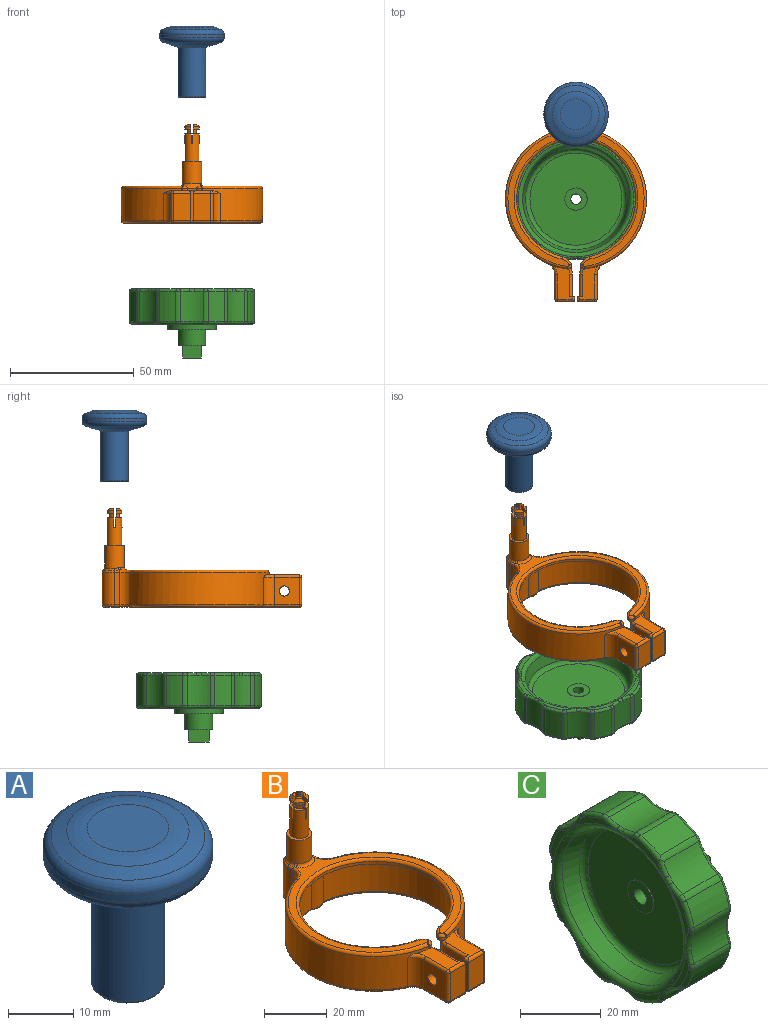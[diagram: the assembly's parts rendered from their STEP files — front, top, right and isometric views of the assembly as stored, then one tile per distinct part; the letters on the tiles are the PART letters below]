
ASSEMBLY  parts=3 mates=2
PART A: 20 faces, bbox 28.1x28.1x29 mm
  f0: cylinder r=4.1mm len=8.2mm, axis (0,0,-1), area 195.8mm2, adj f13,f14
  f1: plane 10.4x10.4mm, normal (0,0,-1), area 21.3mm2, adj f14,f15
  f2: cylinder r=5.6mm len=19.8mm, axis (0,0,-1), area 696.6mm2, adj f15,f16
  f3: sphere r=30mm, area 343.4mm2, adj f16,f17
  f4: cylinder r=13mm len=26mm, axis (0,0,-1), area 122.3mm2, adj f17,f18
  f5: sphere r=30mm, area 171.9mm2, adj f18,f19
  f6: plane 12.49x12.49mm, normal (0,0,1), area 122.5mm2, adj f19
  f7: plane 6.2x6.2mm, normal (0,0,-1), area 30.2mm2, adj f8
  f8: cylinder r=3.1mm len=6.2mm, axis (0,0,-1), area 62.3mm2, adj f7,f9
  f9: plane 6.2x6.2mm, normal (0,0,1), area 16.3mm2, adj f8,f10
  f10: cylinder r=2.1mm len=4.2mm, axis (0,0,-1), area 10.6mm2, adj f9,f11
  f11: cone r=3.1mm half-angle=45deg, axis (0,0,-1), area 23.1mm2, adj f10,f12
  f12: cylinder r=3.1mm len=11mm, axis (0,0,-1), area 214.3mm2, adj f11,f13
  f13: plane 8.2x8.2mm, normal (0,0,-1), area 22.6mm2, adj f0,f12
  f14: torus R=4.5mm, axis (0,0,-1), area 16.8mm2, adj f0,f1
  f15: torus R=5.2mm, axis (0,0,-1), area 21.5mm2, adj f1,f2
  f16: torus R=6mm, axis (0,0,1), area 19.7mm2, adj f2,f3
  f17: torus R=11mm, axis (0,0,1), area 184.4mm2, adj f3,f4
  f18: torus R=11mm, axis (0,0,-1), area 184.4mm2, adj f4,f5
  f19: torus R=6.24mm, axis (0,0,-1), area 156mm2, adj f5,f6
PART B: 154 faces, bbox 61.7x81x40.1 mm
  f0: plane 2.34x2.34mm, normal (0,0,-1), area 2.7mm2, adj f3,f6,f138,f139
  f1: plane 2.34x2.34mm, normal (0,0,-1), area 2.7mm2, adj f4,f7,f142,f143
  f2: plane 2.34x2.34mm, normal (0,0,-1), area 2.7mm2, adj f5,f8,f144,f145
  f3: cylinder r=2mm len=2mm, axis (0,0,-1), area 3.9mm2, adj f0,f27,f138,f139,f150,f152
  f4: cylinder r=2mm len=2mm, axis (0,0,-1), area 3.9mm2, adj f1,f28,f142,f143,f146,f147
  f5: cylinder r=2mm len=2mm, axis (0,0,-1), area 3.9mm2, adj f2,f29,f144,f145,f151,f153
  f6: cylinder r=3mm len=2.34mm, axis (0,0,-1), area 3.5mm2, adj f0,f9,f138,f139
  f7: cylinder r=3mm len=2.34mm, axis (0,0,-1), area 3.5mm2, adj f1,f10,f142,f143
  f8: cylinder r=3mm len=2.34mm, axis (0,0,-1), area 3.5mm2, adj f2,f11,f144,f145
  f9: cone r=2mm half-angle=45deg, axis (0,0,-1), area 3.8mm2, adj f6,f12,f138,f139
  f10: cone r=2mm half-angle=45deg, axis (0,0,-1), area 3.8mm2, adj f7,f13,f142,f143
  f11: cone r=2mm half-angle=45deg, axis (0,0,-1), area 3.8mm2, adj f8,f14,f144,f145
  f12: plane 1.31x1.31mm, normal (0,0,1), area 1mm2, adj f9,f25,f138,f139
  f13: plane 1.31x1.31mm, normal (0,0,1), area 1mm2, adj f10,f24,f142,f143
  f14: plane 1.31x1.31mm, normal (0,0,1), area 1mm2, adj f11,f23,f144,f145
  f15: plane 4x1.77mm, normal (0,1,0), area 7.1mm2, adj f25,f26,f27,f136
  f16: plane 4x1.77mm, normal (1,0,0), area 7.1mm2, adj f25,f26,f27,f136
  f17: plane 4x1.77mm, normal (-1,0,0), area 7.1mm2, adj f26,f131,f136,f137
  f18: plane 4x1.77mm, normal (0,1,0), area 7.1mm2, adj f26,f131,f136,f137
  f19: plane 4x1.77mm, normal (0,-1,0), area 7.1mm2, adj f24,f26,f28,f136
  f20: plane 4x1.77mm, normal (-1,0,0), area 7.1mm2, adj f24,f26,f28,f136
  f21: plane 4x1.77mm, normal (1,0,0), area 7.1mm2, adj f23,f26,f29,f136
  f22: plane 4x1.77mm, normal (0,-1,0), area 7.1mm2, adj f23,f26,f29,f136
  f23: cylinder r=1.25mm len=8mm, axis (0,0,1), area 8.7mm2, adj f14,f21,f22,f29,f136,f144,f145,f151
  f24: cylinder r=1.25mm len=8mm, axis (0,0,1), area 8.7mm2, adj f13,f19,f20,f28,f136,f142,f143,f146
  f25: cylinder r=1.25mm len=8mm, axis (0,0,1), area 8.7mm2, adj f12,f15,f16,f27,f136,f138,f139,f150
  f26: cylinder r=3mm len=11mm, axis (0,0,-1), area 199.3mm2, adj f15,f16,f17,f18,f19,f20,f21,f22
  f27: plane 2.74x2.74mm, normal (0,0,1), area 3.5mm2, adj f3,f15,f16,f25,f26,f150,f152
  f28: plane 2.74x2.74mm, normal (0,0,1), area 3.5mm2, adj f4,f19,f20,f24,f26,f146,f147
  f29: plane 2.74x2.74mm, normal (0,0,1), area 3.5mm2, adj f5,f21,f22,f23,f26,f151,f153
  f30: cylinder r=1.5mm len=2.11mm, axis (0,0,1), area 3.6mm2, adj f32,f49,f59,f60,f64,f69,f117
  f31: cylinder r=1.5mm len=2.11mm, axis (0,0,1), area 3.6mm2, adj f33,f45,f59,f61,f62,f77,f119
  f32: plane 13.34x7.12mm, normal (0,0,1), area 64.1mm2, adj f30,f51,f56,f60,f80,f81,f82,f83
  f33: plane 13.34x7.12mm, normal (0,0,1), area 64.1mm2, adj f31,f38,f43,f61,f95,f96,f98,f99
  f34: plane 13x2.03mm, normal (1,0,0), area 26.4mm2, adj f35,f57,f70,f93
  f35: cylinder r=5mm len=13mm, axis (0,0,-1), area 204.2mm2, adj f34,f36,f72,f94
  f36: plane 13x2.03mm, normal (-1,0,0), area 26.4mm2, adj f35,f37,f74,f97
  f37: cylinder r=5mm len=13mm, axis (0,0,-1), area 82.4mm2, adj f36,f38,f76,f100
  f38: cylinder r=28.5mm len=55.41mm, axis (0,0,-1), area 907.2mm2, adj f33,f37,f39,f61,f78,f95,f103
  f39: cylinder r=5mm len=11mm, axis (0,0,-1), area 63.6mm2, adj f38,f40,f95,f106
  f40: plane 11x9.84mm, normal (-1,0,0), area 95mm2, adj f39,f98,f104,f108,f129
  f41: plane 11x7mm, normal (0,-1,0), area 77mm2, adj f42,f99,f104,f105
  f42: plane 11x2mm, normal (1,0,0), area 22mm2, adj f41,f43,f96,f102
  f43: plane 13x2mm, normal (0,1,0), area 13mm2, adj f33,f42,f44,f58,f96,f102,f109,f118
  f44: plane 11x9.19mm, normal (1,0,0), area 87.9mm2, adj f43,f45,f109,f118,f129
  f45: cylinder r=5mm len=12mm, axis (0,0,-1), area 79mm2, adj f31,f44,f46,f59,f110,f119
  f46: cylinder r=26mm len=51.27mm, axis (0,0,-1), area 880.7mm2, adj f45,f47,f59,f111
  f47: cylinder r=5mm len=12mm, axis (0,0,-1), area 71mm2, adj f46,f48,f59,f112
  f48: cylinder r=26mm len=51.27mm, axis (0,0,-1), area 880.7mm2, adj f47,f49,f59,f113
  f49: cylinder r=5mm len=12mm, axis (0,0,-1), area 79mm2, adj f30,f48,f50,f59,f114,f117
  f50: plane 11x9.19mm, normal (-1,0,0), area 87.9mm2, adj f49,f51,f115,f116,f128
  f51: plane 13x2mm, normal (0,1,0), area 13mm2, adj f32,f50,f52,f58,f80,f84,f115,f116
  f52: plane 11x2mm, normal (-1,0,0), area 22mm2, adj f51,f53,f80,f84
  f53: plane 11x7mm, normal (0,-1,0), area 77mm2, adj f52,f82,f86,f87
  f54: plane 11x9.84mm, normal (1,0,0), area 95mm2, adj f55,f83,f87,f89,f128
  f55: cylinder r=5mm len=11mm, axis (0,0,-1), area 63.6mm2, adj f54,f56,f81,f90
  f56: cylinder r=28.5mm len=55.41mm, axis (0,0,-1), area 907.2mm2, adj f32,f55,f57,f60,f66,f81,f91
  f57: cylinder r=5mm len=13mm, axis (0,0,-1), area 82.4mm2, adj f34,f56,f68,f92
  f58: plane 78.5x55mm, normal (0,0,-1), area 311.2mm2, adj f43,f51,f84,f86,f89,f90,f91,f92
  f59: plane 53.67x52mm, normal (0,0,-1), area 302.9mm2, adj f30,f31,f45,f46,f47,f48,f49,f62
  f60: cylinder r=3mm len=1mm, axis (0,0,-1), area 0.4mm2, adj f30,f32,f56,f67
  f61: cylinder r=3mm len=1mm, axis (0,0,-1), area 0.4mm2, adj f31,f33,f38,f79
  f62: cylinder r=5mm len=3.45mm, axis (0,0,-1), area 4.6mm2, adj f31,f59,f63,f75
  f63: cylinder r=24mm len=48mm, axis (0,0,-1), area 139.9mm2, adj f59,f62,f64,f73
  f64: cylinder r=5mm len=3.45mm, axis (0,0,-1), area 4.6mm2, adj f30,f59,f63,f71
  f65: plane 58.43x55mm, normal (0,0,1), area 421.1mm2, adj f66,f67,f68,f69,f71,f73,f75,f76
  f66: torus R=27.5mm, axis (0,0,1), area 119.1mm2, adj f56,f65,f67,f68
  f67: torus R=4mm, axis (0,0,1), area 0.7mm2, adj f60,f65,f66,f69
  f68: torus R=6mm, axis (0,0,1), area 10.6mm2, adj f57,f65,f66,f70,f125
  f69: torus R=0.5mm, axis (0,0,1), area 4mm2, adj f30,f65,f67,f71
  f70: cylinder r=1mm len=2.03mm, axis (0,-1,0), area 2.4mm2, adj f34,f68,f72,f127
  f71: torus R=4mm, axis (0,0,1), area 6.7mm2, adj f64,f65,f69,f73
  f72: torus R=4mm, axis (0,0,1), area 15.9mm2, adj f35,f70,f74,f126
  f73: torus R=25mm, axis (0,0,1), area 223.2mm2, adj f63,f65,f71,f75
  f74: cylinder r=1mm len=2.03mm, axis (0,1,0), area 2.4mm2, adj f36,f72,f76,f124
  f75: torus R=4mm, axis (0,0,1), area 6.7mm2, adj f62,f65,f73,f77
  f76: torus R=6mm, axis (0,0,1), area 10.6mm2, adj f37,f65,f74,f78,f122
  f77: torus R=0.5mm, axis (0,0,1), area 4mm2, adj f31,f65,f75,f79
  f78: torus R=27.5mm, axis (0,0,1), area 119.1mm2, adj f38,f65,f76,f79
  f79: torus R=4mm, axis (0,0,1), area 0.7mm2, adj f61,f65,f77,f78
  f80: cylinder r=1mm len=2mm, axis (0,1,0), area 2.4mm2, adj f32,f51,f52,f82
  f81: torus R=6mm, axis (0,0,1), area 7.4mm2, adj f32,f55,f56,f83
  f82: cylinder r=1mm len=7mm, axis (-1,0,0), area 10.2mm2, adj f32,f53,f80,f85
  f83: cylinder r=1mm len=9.84mm, axis (0,-1,0), area 15.5mm2, adj f32,f54,f81,f85
  f84: cylinder r=1mm len=2mm, axis (0,-1,0), area 2.4mm2, adj f51,f52,f58,f86
  f85: sphere r=1mm, area 1.6mm2, adj f82,f83,f87
  f86: cylinder r=1mm len=7mm, axis (1,0,0), area 10.2mm2, adj f53,f58,f84,f88
  f87: cylinder r=1mm len=11mm, axis (0,0,-1), area 17.3mm2, adj f53,f54,f85,f88
  f88: sphere r=1mm, area 1.6mm2, adj f86,f87,f89
  f89: cylinder r=1mm len=9.84mm, axis (0,1,0), area 15.5mm2, adj f54,f58,f88,f90
  f90: torus R=6mm, axis (0,0,1), area 9.7mm2, adj f55,f58,f89,f91
  f91: torus R=27.5mm, axis (0,0,1), area 107.1mm2, adj f56,f58,f90,f92
  f92: torus R=6mm, axis (0,0,1), area 10.7mm2, adj f57,f58,f91,f93
  f93: cylinder r=1mm len=2.03mm, axis (0,1,0), area 3.2mm2, adj f34,f58,f92,f94
  f94: torus R=4mm, axis (0,0,1), area 22.9mm2, adj f35,f58,f93,f97
  f95: torus R=6mm, axis (0,0,1), area 7.4mm2, adj f33,f38,f39,f98
  f96: cylinder r=1mm len=2mm, axis (0,-1,0), area 2.4mm2, adj f33,f42,f43,f99
  f97: cylinder r=1mm len=2.03mm, axis (0,-1,0), area 3.2mm2, adj f36,f58,f94,f100
  f98: cylinder r=1mm len=9.84mm, axis (0,1,0), area 15.5mm2, adj f33,f40,f95,f101
  f99: cylinder r=1mm len=7mm, axis (-1,0,0), area 10.2mm2, adj f33,f41,f96,f101
  f100: torus R=6mm, axis (0,0,1), area 10.7mm2, adj f37,f58,f97,f103
  f101: sphere r=1mm, area 1.6mm2, adj f98,f99,f104
  f102: cylinder r=1mm len=2mm, axis (0,1,0), area 2.4mm2, adj f42,f43,f58,f105
  f103: torus R=27.5mm, axis (0,0,1), area 107.1mm2, adj f38,f58,f100,f106
  f104: cylinder r=1mm len=11mm, axis (0,0,-1), area 17.3mm2, adj f40,f41,f101,f107
  f105: cylinder r=1mm len=7mm, axis (1,0,0), area 10.2mm2, adj f41,f58,f102,f107
  f106: torus R=6mm, axis (0,0,1), area 9.7mm2, adj f39,f58,f103,f108
  f107: sphere r=1mm, area 1.6mm2, adj f104,f105,f108
  f108: cylinder r=1mm len=9.84mm, axis (0,-1,0), area 15.5mm2, adj f40,f58,f106,f107
  f109: cylinder r=1mm len=9.19mm, axis (0,1,0), area 14.4mm2, adj f43,f44,f58,f110
  f110: torus R=4mm, axis (0,0,1), area 9.9mm2, adj f45,f58,f109,f111
  f111: torus R=27mm, axis (0,0,1), area 117.2mm2, adj f46,f58,f110,f112
  f112: torus R=4mm, axis (0,0,1), area 9.2mm2, adj f47,f58,f111,f113
  f113: torus R=27mm, axis (0,0,1), area 117.2mm2, adj f48,f58,f112,f114
  f114: torus R=4mm, axis (0,0,1), area 9.9mm2, adj f49,f58,f113,f115
  f115: cylinder r=1mm len=9.19mm, axis (0,-1,0), area 14.4mm2, adj f50,f51,f58,f114
  f116: cylinder r=1mm len=9.19mm, axis (0,1,0), area 14.4mm2, adj f32,f50,f51,f117
  f117: torus R=4mm, axis (0,0,1), area 3.7mm2, adj f30,f32,f49,f116
  f118: cylinder r=1mm len=9.19mm, axis (0,-1,0), area 14.4mm2, adj f33,f43,f44,f119
  f119: torus R=4mm, axis (0,0,1), area 3.7mm2, adj f31,f33,f45,f118
  f120: cylinder r=4mm len=9.27mm, axis (0,0,-1), area 230.2mm2, adj f121,f122,f123,f124,f125,f126,f127
  f121: plane 8x8mm, normal (0,0,1), area 22mm2, adj f26,f120
  f122: bspline ~1.78x1.24mm, area 1.2mm2, adj f76,f120,f123,f124
  f123: torus R=5mm, axis (0,0,1), area 13mm2, adj f65,f120,f122,f125
  f124: bspline ~3.16x1.25mm, area 2.1mm2, adj f74,f120,f122,f126
  f125: bspline ~1.77x1.33mm, area 1.2mm2, adj f68,f120,f123,f127
  f126: torus R=5mm, axis (0,0,1), area 13.7mm2, adj f72,f120,f124,f127
  f127: bspline ~3.26x1.1mm, area 2.1mm2, adj f70,f120,f125,f126
  f128: cylinder r=2.05mm len=7mm, axis (-1,0,0), area 90.2mm2, adj f50,f54
  f129: cylinder r=2.05mm len=7mm, axis (-1,0,0), area 90.2mm2, adj f40,f44
  f130: plane 2.34x2.34mm, normal (0,0,-1), area 2.7mm2, adj f132,f133,f140,f141
  f131: plane 2.74x2.74mm, normal (0,0,1), area 3.5mm2, adj f17,f18,f26,f132,f137,f148,f149
  f132: cylinder r=2mm len=2mm, axis (0,0,-1), area 3.9mm2, adj f130,f131,f140,f141,f148,f149
  f133: cylinder r=3mm len=2.34mm, axis (0,0,-1), area 3.5mm2, adj f130,f134,f140,f141
  f134: cone r=2mm half-angle=45deg, axis (0,0,-1), area 3.8mm2, adj f133,f135,f140,f141
  f135: plane 1.31x1.31mm, normal (0,0,1), area 1mm2, adj f134,f137,f140,f141
  f136: plane 6x6mm, normal (0,0,1), area 8.4mm2, adj f15,f16,f17,f18,f19,f20,f21,f22
  f137: cylinder r=1.25mm len=8mm, axis (0,0,1), area 8.7mm2, adj f17,f18,f131,f135,f136,f140,f141,f148
  f138: plane 3.75x1.9mm, normal (0,1,0), area 4.6mm2, adj f0,f3,f6,f9,f12,f25,f152
  f139: plane 3.75x1.9mm, normal (1,0,0), area 4.6mm2, adj f0,f3,f6,f9,f12,f25,f150
  f140: plane 3.75x1.9mm, normal (0,1,0), area 4.6mm2, adj f130,f132,f133,f134,f135,f137,f148
  f141: plane 3.75x1.9mm, normal (-1,0,0), area 4.6mm2, adj f130,f132,f133,f134,f135,f137,f149
  f142: plane 3.75x1.9mm, normal (0,-1,0), area 4.6mm2, adj f1,f4,f7,f10,f13,f24,f147
  f143: plane 3.75x1.9mm, normal (-1,0,0), area 4.6mm2, adj f1,f4,f7,f10,f13,f24,f146
  f144: plane 3.75x1.9mm, normal (1,0,0), area 4.6mm2, adj f2,f5,f8,f11,f14,f23,f151
  f145: plane 3.75x1.9mm, normal (0,-1,0), area 4.6mm2, adj f2,f5,f8,f11,f14,f23,f153
  f146: cylinder r=0.3mm len=0.88mm, axis (0,-1,0), area 0.4mm2, adj f4,f24,f28,f143
  f147: cylinder r=0.3mm len=0.88mm, axis (1,0,0), area 0.4mm2, adj f4,f24,f28,f142
  f148: cylinder r=0.3mm len=0.88mm, axis (-1,0,0), area 0.4mm2, adj f131,f132,f137,f140
  f149: cylinder r=0.3mm len=0.88mm, axis (0,-1,0), area 0.4mm2, adj f131,f132,f137,f141
  f150: cylinder r=0.3mm len=0.88mm, axis (0,1,0), area 0.4mm2, adj f3,f25,f27,f139
  f151: cylinder r=0.3mm len=0.88mm, axis (0,1,0), area 0.4mm2, adj f5,f23,f29,f144
  f152: cylinder r=0.3mm len=0.88mm, axis (-1,0,0), area 0.4mm2, adj f3,f25,f27,f138
  f153: cylinder r=0.3mm len=0.88mm, axis (1,0,0), area 0.4mm2, adj f5,f23,f29,f145
PART C: 144 faces, bbox 28x53.1x53.1 mm
  f0: plane 14.68x7.11mm, normal (-1,0,0), area 19.4mm2, adj f44,f84,f86,f88,f140,f141
  f1: plane 14.68x7.11mm, normal (-1,0,0), area 19.4mm2, adj f44,f76,f78,f80,f134,f135
  f2: plane 14.68x7.11mm, normal (-1,0,0), area 19.4mm2, adj f44,f68,f70,f72,f128,f129
  f3: plane 14.68x7.11mm, normal (-1,0,0), area 19.4mm2, adj f44,f62,f63,f64,f122,f123
  f4: plane 14.68x7.11mm, normal (-1,0,0), area 19.4mm2, adj f44,f67,f69,f71,f119
  f5: plane 14.68x7.11mm, normal (-1,0,0), area 19.4mm2, adj f44,f75,f77,f79,f111,f112
  f6: plane 14.68x7.11mm, normal (-1,0,0), area 19.4mm2, adj f44,f83,f85,f87,f105,f106
  f7: plane 48.53x48.53mm, normal (1,0,0), area 242.3mm2, adj f46,f47,f48,f49,f50,f51,f52,f53
  f8: plane 14.68x7.11mm, normal (-1,0,0), area 19.4mm2, adj f44,f91,f92,f93,f99,f100
  f9: cylinder r=25.99mm len=12.28mm, axis (-1,0,0), area 89.7mm2, adj f49,f69,f115,f118
  f10: cylinder r=25.99mm len=12.28mm, axis (-1,0,0), area 89.7mm2, adj f53,f77,f110,f113
  f11: cylinder r=25.99mm len=12.28mm, axis (-1,0,0), area 89.7mm2, adj f57,f85,f104,f107
  f12: cylinder r=25.99mm len=12.28mm, axis (-1,0,0), area 89.7mm2, adj f61,f93,f98,f101
  f13: cylinder r=25.99mm len=12.28mm, axis (-1,0,0), area 89.7mm2, adj f58,f86,f139,f142
  f14: cylinder r=25.99mm len=12.28mm, axis (-1,0,0), area 89.7mm2, adj f54,f78,f133,f136
  f15: cylinder r=25.99mm len=12.28mm, axis (-1,0,0), area 89.7mm2, adj f50,f70,f127,f130
  f16: plane 7.59x1.47mm, normal (1,0,0), area 7.7mm2, adj f24,f26
  f17: plane 8.3x1.83mm, normal (1,0,0), area 10.5mm2, adj f24,f29
  f18: plane 7.59x1.47mm, normal (1,0,0), area 7.7mm2, adj f24,f28
  f19: cylinder r=25.99mm len=12.28mm, axis (-1,0,0), area 89.7mm2, adj f46,f62,f121,f124
  f20: cylinder r=21.65mm len=43.3mm, axis (1,0,0), area 197.2mm2, adj f94,f95
  f21: plane 41.3x41.3mm, normal (1,0,0), area 940.6mm2, adj f95,f96
  f22: cylinder r=9.77mm len=19.54mm, axis (-1,0,0), area 250.5mm2, adj f23,f96
  f23: plane 19.54x19.54mm, normal (1,0,0), area 200.5mm2, adj f22,f24
  f24: cylinder r=5.62mm len=11.25mm, axis (-1,0,0), area 229.7mm2, adj f16,f17,f18,f23,f25
  f25: plane 8.3x1.83mm, normal (1,0,0), area 10.5mm2, adj f24,f27
  f26: plane 7.59x5mm, normal (0,1,0), area 37.9mm2, adj f16,f27,f29,f30
  f27: plane 8.3x5mm, normal (0,0,1), area 41.5mm2, adj f25,f26,f28,f30
  f28: plane 7.59x5mm, normal (0,-1,0), area 37.9mm2, adj f18,f27,f29,f30
  f29: plane 8.3x5mm, normal (0,0,-1), area 41.5mm2, adj f17,f26,f28,f30
  f30: plane 8.3x7.59mm, normal (1,0,0), area 49.2mm2, adj f26,f27,f28,f29,f43
  f31: plane 37.18x37.18mm, normal (-1,0,0), area 1022.1mm2, adj f41,f45
  f32: cone r=20mm half-angle=13.9deg, axis (-1,0,0), area 644.9mm2, adj f44,f45
  f33: cylinder r=13mm len=12.28mm, axis (-1,0,0), area 117mm2, adj f47,f63,f65,f67,f118,f124
  f34: cylinder r=13mm len=12.28mm, axis (-1,0,0), area 117mm2, adj f48,f64,f66,f68,f121,f130
  f35: cylinder r=13mm len=12.28mm, axis (-1,0,0), area 117mm2, adj f52,f72,f74,f76,f127,f136
  f36: cylinder r=13mm len=12.28mm, axis (-1,0,0), area 117mm2, adj f56,f80,f82,f84,f133,f142
  f37: cylinder r=13mm len=12.28mm, axis (-1,0,0), area 117mm2, adj f60,f88,f90,f92,f101,f139
  f38: cylinder r=13mm len=12.28mm, axis (-1,0,0), area 117mm2, adj f59,f87,f89,f91,f98,f107
  f39: cylinder r=13mm len=12.28mm, axis (-1,0,0), area 117mm2, adj f55,f79,f81,f83,f104,f113
  f40: cylinder r=13mm len=12.28mm, axis (-1,0,0), area 117mm2, adj f51,f71,f73,f75,f110,f115
  f41: cylinder r=4.5mm len=9mm, axis (1,0,0), area 5.7mm2, adj f31,f42
  f42: plane 9x9mm, normal (-1,0,0), area 49.8mm2, adj f41,f43
  f43: cylinder r=2.1mm len=20.61mm, axis (-1,0,0), area 271.9mm2, adj f30,f42
  f44: torus R=23.26mm, axis (1,0,0), area 332.7mm2, adj f0,f1,f2,f3,f4,f5,f6,f8
  f45: torus R=18.59mm, axis (1,0,0), area 294.9mm2, adj f31,f32
  f46: torus R=24.99mm, axis (1,0,0), area 11.3mm2, adj f7,f19,f120,f125
  f47: torus R=14mm, axis (1,0,0), area 15.4mm2, adj f7,f33,f117,f125
  f48: torus R=14mm, axis (1,0,0), area 15.4mm2, adj f7,f34,f120,f131
  f49: torus R=24.99mm, axis (1,0,0), area 11.3mm2, adj f7,f9,f116,f117
  f50: torus R=24.99mm, axis (1,0,0), area 11.3mm2, adj f7,f15,f126,f131
  f51: torus R=14mm, axis (1,0,0), area 15.4mm2, adj f7,f40,f109,f116
  f52: torus R=14mm, axis (1,0,0), area 15.4mm2, adj f7,f35,f126,f137
  f53: torus R=24.99mm, axis (1,0,0), area 11.3mm2, adj f7,f10,f109,f114
  f54: torus R=24.99mm, axis (1,0,0), area 11.3mm2, adj f7,f14,f132,f137
  f55: torus R=14mm, axis (1,0,0), area 15.4mm2, adj f7,f39,f103,f114
  f56: torus R=14mm, axis (1,0,0), area 15.4mm2, adj f7,f36,f132,f143
  f57: torus R=24.99mm, axis (1,0,0), area 11.3mm2, adj f7,f11,f103,f108
  f58: torus R=24.99mm, axis (1,0,0), area 11.3mm2, adj f7,f13,f138,f143
  f59: torus R=14mm, axis (1,0,0), area 15.4mm2, adj f7,f38,f97,f108
  f60: torus R=14mm, axis (1,0,0), area 15.4mm2, adj f7,f37,f102,f138
  f61: torus R=24.99mm, axis (1,0,0), area 11.3mm2, adj f7,f12,f97,f102
  f62: torus R=24.99mm, axis (1,0,0), area 11.3mm2, adj f3,f19,f122,f123
  f63: torus R=14mm, axis (1,0,0), area 6.2mm2, adj f3,f33,f65,f123
  f64: torus R=14mm, axis (1,0,0), area 6.2mm2, adj f3,f34,f66,f122
  f65: bspline ~3.13x1.17mm, area 3.2mm2, adj f33,f44,f63,f67
  f66: bspline ~2.57x2.48mm, area 3.2mm2, adj f34,f44,f64,f68
  f67: torus R=14mm, axis (1,0,0), area 6.2mm2, adj f4,f33,f65,f119
  f68: torus R=14mm, axis (1,0,0), area 6.2mm2, adj f2,f34,f66,f129
  f69: torus R=24.99mm, axis (1,0,0), area 12.4mm2, adj f4,f9,f71,f115,f119
  f70: torus R=24.99mm, axis (1,0,0), area 11.3mm2, adj f2,f15,f128,f129
  f71: torus R=14mm, axis (1,0,0), area 7.1mm2, adj f4,f40,f69,f73,f115
  f72: torus R=14mm, axis (1,0,0), area 6.2mm2, adj f2,f35,f74,f128
  f73: bspline ~2.57x2.48mm, area 3.2mm2, adj f40,f44,f71,f75
  f74: bspline ~3.13x1.17mm, area 3.2mm2, adj f35,f44,f72,f76
  f75: torus R=14mm, axis (1,0,0), area 6.2mm2, adj f5,f40,f73,f111
  f76: torus R=14mm, axis (1,0,0), area 6.2mm2, adj f1,f35,f74,f135
  f77: torus R=24.99mm, axis (1,0,0), area 11.3mm2, adj f5,f10,f111,f112
  f78: torus R=24.99mm, axis (1,0,0), area 11.3mm2, adj f1,f14,f134,f135
  f79: torus R=14mm, axis (1,0,0), area 6.2mm2, adj f5,f39,f81,f112
  f80: torus R=14mm, axis (1,0,0), area 6.2mm2, adj f1,f36,f82,f134
  f81: bspline ~3.13x1.17mm, area 3.2mm2, adj f39,f44,f79,f83
  f82: bspline ~2.57x2.48mm, area 3.2mm2, adj f36,f44,f80,f84
  f83: torus R=14mm, axis (1,0,0), area 6.2mm2, adj f6,f39,f81,f105
  f84: torus R=14mm, axis (1,0,0), area 6.2mm2, adj f0,f36,f82,f141
  f85: torus R=24.99mm, axis (1,0,0), area 11.3mm2, adj f6,f11,f105,f106
  f86: torus R=24.99mm, axis (1,0,0), area 11.3mm2, adj f0,f13,f140,f141
  f87: torus R=14mm, axis (1,0,0), area 6.2mm2, adj f6,f38,f89,f106
  f88: torus R=14mm, axis (1,0,0), area 6.2mm2, adj f0,f37,f90,f140
  f89: bspline ~2.57x2.48mm, area 3.2mm2, adj f38,f44,f87,f91
  f90: bspline ~3.13x1.17mm, area 3.2mm2, adj f37,f44,f88,f92
  f91: torus R=14mm, axis (1,0,0), area 6.2mm2, adj f8,f38,f89,f99
  f92: torus R=14mm, axis (1,0,0), area 6.2mm2, adj f8,f37,f90,f100
  f93: torus R=24.99mm, axis (1,0,0), area 11.3mm2, adj f8,f12,f99,f100
  f94: torus R=22.65mm, axis (1,0,0), area 217.3mm2, adj f7,f20
  f95: torus R=20.65mm, axis (1,0,0), area 210.1mm2, adj f20,f21
  f96: torus R=11.27mm, axis (1,0,0), area 152.7mm2, adj f21,f22
  f97: torus R=2mm, axis (1,0,0), area 2.6mm2, adj f7,f59,f61,f98
  f98: cylinder r=3mm len=12.28mm, axis (1,0,0), area 22.8mm2, adj f12,f38,f97,f99
  f99: torus R=2mm, axis (1,0,0), area 2.6mm2, adj f8,f91,f93,f98
  f100: torus R=2mm, axis (1,0,0), area 2.6mm2, adj f8,f92,f93,f101
  f101: cylinder r=3mm len=12.28mm, axis (-1,0,0), area 22.8mm2, adj f12,f37,f100,f102
  f102: torus R=2mm, axis (1,0,0), area 2.6mm2, adj f7,f60,f61,f101
  f103: torus R=2mm, axis (1,0,0), area 2.6mm2, adj f7,f55,f57,f104
  f104: cylinder r=3mm len=12.28mm, axis (1,0,0), area 22.8mm2, adj f11,f39,f103,f105
  f105: torus R=2mm, axis (1,0,0), area 2.6mm2, adj f6,f83,f85,f104
  f106: torus R=2mm, axis (1,0,0), area 2.6mm2, adj f6,f85,f87,f107
  f107: cylinder r=3mm len=12.28mm, axis (-1,0,0), area 22.8mm2, adj f11,f38,f106,f108
  f108: torus R=2mm, axis (1,0,0), area 2.6mm2, adj f7,f57,f59,f107
  f109: torus R=2mm, axis (1,0,0), area 2.6mm2, adj f7,f51,f53,f110
  f110: cylinder r=3mm len=12.28mm, axis (1,0,0), area 22.8mm2, adj f10,f40,f109,f111
  f111: torus R=2mm, axis (1,0,0), area 2.6mm2, adj f5,f75,f77,f110
  f112: torus R=2mm, axis (1,0,0), area 2.6mm2, adj f5,f77,f79,f113
  f113: cylinder r=3mm len=12.28mm, axis (-1,0,0), area 22.8mm2, adj f10,f39,f112,f114
  f114: torus R=2mm, axis (1,0,0), area 2.6mm2, adj f7,f53,f55,f113
  f115: cylinder r=3mm len=12.8mm, axis (-1,0,0), area 23.3mm2, adj f9,f40,f69,f71,f116
  f116: torus R=2mm, axis (1,0,0), area 2.6mm2, adj f7,f49,f51,f115
  f117: torus R=2mm, axis (1,0,0), area 2.6mm2, adj f7,f47,f49,f118
  f118: cylinder r=3mm len=12.28mm, axis (1,0,0), area 22.8mm2, adj f9,f33,f117,f119
  f119: torus R=2mm, axis (1,0,0), area 2.6mm2, adj f4,f67,f69,f118
  f120: torus R=2mm, axis (1,0,0), area 2.6mm2, adj f7,f46,f48,f121
  f121: cylinder r=3mm len=12.28mm, axis (1,0,0), area 22.8mm2, adj f19,f34,f120,f122
  f122: torus R=2mm, axis (1,0,0), area 2.6mm2, adj f3,f62,f64,f121
  f123: torus R=2mm, axis (1,0,0), area 2.6mm2, adj f3,f62,f63,f124
  f124: cylinder r=3mm len=12.28mm, axis (-1,0,0), area 22.8mm2, adj f19,f33,f123,f125
  f125: torus R=2mm, axis (1,0,0), area 2.6mm2, adj f7,f46,f47,f124
  f126: torus R=2mm, axis (1,0,0), area 2.6mm2, adj f7,f50,f52,f127
  f127: cylinder r=3mm len=12.28mm, axis (1,0,0), area 22.8mm2, adj f15,f35,f126,f128
  f128: torus R=2mm, axis (1,0,0), area 2.6mm2, adj f2,f70,f72,f127
  f129: torus R=2mm, axis (1,0,0), area 2.6mm2, adj f2,f68,f70,f130
  f130: cylinder r=3mm len=12.28mm, axis (-1,0,0), area 22.8mm2, adj f15,f34,f129,f131
  f131: torus R=2mm, axis (1,0,0), area 2.6mm2, adj f7,f48,f50,f130
  f132: torus R=2mm, axis (1,0,0), area 2.6mm2, adj f7,f54,f56,f133
  f133: cylinder r=3mm len=12.28mm, axis (1,0,0), area 22.8mm2, adj f14,f36,f132,f134
  f134: torus R=2mm, axis (1,0,0), area 2.6mm2, adj f1,f78,f80,f133
  f135: torus R=2mm, axis (1,0,0), area 2.6mm2, adj f1,f76,f78,f136
  f136: cylinder r=3mm len=12.28mm, axis (-1,0,0), area 22.8mm2, adj f14,f35,f135,f137
  f137: torus R=2mm, axis (1,0,0), area 2.6mm2, adj f7,f52,f54,f136
  f138: torus R=2mm, axis (1,0,0), area 2.6mm2, adj f7,f58,f60,f139
  f139: cylinder r=3mm len=12.28mm, axis (1,0,0), area 22.8mm2, adj f13,f37,f138,f140
  f140: torus R=2mm, axis (1,0,0), area 2.6mm2, adj f0,f86,f88,f139
  f141: torus R=2mm, axis (1,0,0), area 2.6mm2, adj f0,f84,f86,f142
  f142: cylinder r=3mm len=12.28mm, axis (-1,0,0), area 22.8mm2, adj f13,f36,f141,f143
  f143: torus R=2mm, axis (1,0,0), area 2.6mm2, adj f7,f56,f58,f142
PLACE A t=(-6.88,53.74,47.88)mm
PLACE B t=(-6.88,19.74,-2.7)mm
PLACE C rot(axis=(0,1,0),90deg) t=(-6.88,19.74,-29.21)mm
MATE cylindrical C.f9 <-> B.f46  axis (0,0,1) through (-6.88,19.74,-30.21)mm
MATE cylindrical A.f0 <-> B.f3  axis (0,0,-1) through (-6.88,53.74,55.88)mm
